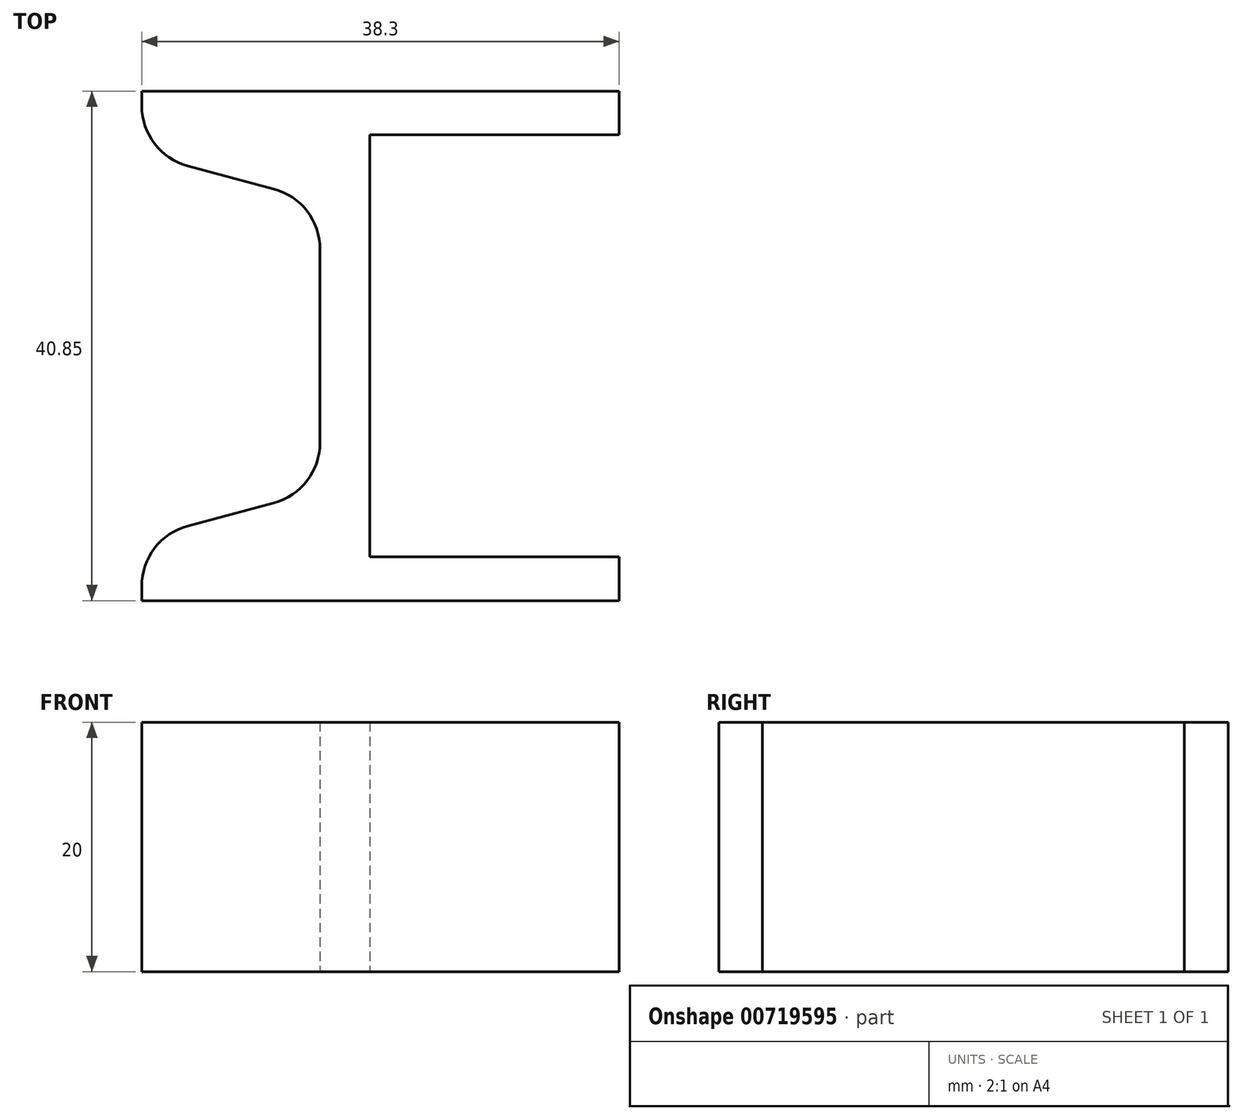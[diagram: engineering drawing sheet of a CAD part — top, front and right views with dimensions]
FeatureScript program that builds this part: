
annotation { "Feature Type Name" : "Feature", "Feature Type Description" : "" }
export const myFeature = defineFeature(function(context is Context, id is Id, definition is map)
    precondition{}
    {
        {
            var Q0;
            Q0=qCreatedBy(makeId("Top.planeOp"),FACE);
            var sketch = newSketch(context, id + "F0", { "sketchPlane" : qUnion([Q0])});
            skLineSegment(sketch, "E0", {"start": v(20, 0) * mm, "end": v(0, 0) * mm});
            skLineSegment(sketch, "E1", {"start": v(0, 0) * mm, "end": v(0, 33.85) * mm});
            skLineSegment(sketch, "E2", {"start": v(0, 33.85) * mm, "end": v(20, 33.85) * mm});
            skLineSegment(sketch, "E3", {"start": v(-18.3, 37.35) * mm, "end": v(-18.3, -3.5) * mm, "construction": true});
            skLineSegment(sketch, "E4", {"start": v(20, 37.35) * mm, "end": v(-18.3, 37.35) * mm});
            skLineSegment(sketch, "E5", {"start": v(-18.3, -3.5) * mm, "end": v(20, -3.5) * mm});
            skLineSegment(sketch, "E6", {"start": v(0, 16.93) * mm, "end": v(-18.3, 16.93) * mm, "construction": true});
            skLineSegment(sketch, "E7", {"start": v(-14.6, 31.36) * mm, "end": v(-7.7, 29.51) * mm});
            skLineSegment(sketch, "E8", {"start": v(-4, 24.68) * mm, "end": v(-4, 16.93) * mm});
            skLineSegment(sketch, "E9", {"start": v(-18.3, 36.19) * mm, "end": v(-18.3, 37.35) * mm});
            skPoint(sketch, "E10.visualSharp", {"position": v(-18.3, 32.35) * mm});
            skArc(sketch, "E10.filletArc", {"start": v(-18.3, 36.19) * mm, "mid": v(-17.27, 33.14) * mm, "end": v(-14.6, 31.36) * mm});
            skPoint(sketch, "E11.visualSharp", {"position": v(-4, 28.52) * mm});
            skArc(sketch, "E11.filletArc", {"start": v(-4, 24.68) * mm, "mid": v(-5.03, 27.73) * mm, "end": v(-7.7, 29.51) * mm});
            skLineSegment(sketch, "E12.MirrorCS", {"start": v(-4, 9.17) * mm, "end": v(-4, 16.93) * mm});
            skArc(sketch, "E13.MirrorCS", {"start": v(-4, 9.17) * mm, "mid": v(-5.03, 6.12) * mm, "end": v(-7.7, 4.34) * mm});
            skLineSegment(sketch, "E14.MirrorCS", {"start": v(-14.6, 2.5) * mm, "end": v(-7.7, 4.34) * mm});
            skArc(sketch, "E15.MirrorCS", {"start": v(-18.3, -2.34) * mm, "mid": v(-17.27, 0.7) * mm, "end": v(-14.6, 2.5) * mm});
            skLineSegment(sketch, "E16", {"start": v(-18.3, -2.34) * mm, "end": v(-18.3, -3.5) * mm});
            skLineSegment(sketch, "E17", {"start": v(20, 37.35) * mm, "end": v(20, 33.85) * mm});
            skLineSegment(sketch, "E18", {"start": v(20, 0) * mm, "end": v(20, -3.5) * mm});
            skSolve(sketch);
        }
        {
            var Q0;
            Q0=makeQuery(id+"F0.imprint","IMPRINT",FACE,{"disambiguationData":[TD([[makeQuery(id+"F0.imprint","IMPRINT",EDGE,{"derivedFrom":sQuery(id+"F0.wireOp",EDGE,"E0")}),1.0]])]});
            extrude(context, id + "F1", {"entities" : qUnion([Q0]), "depth" : 20 * mm, "offsetDistance" : 25 * mm});
        }
    });
